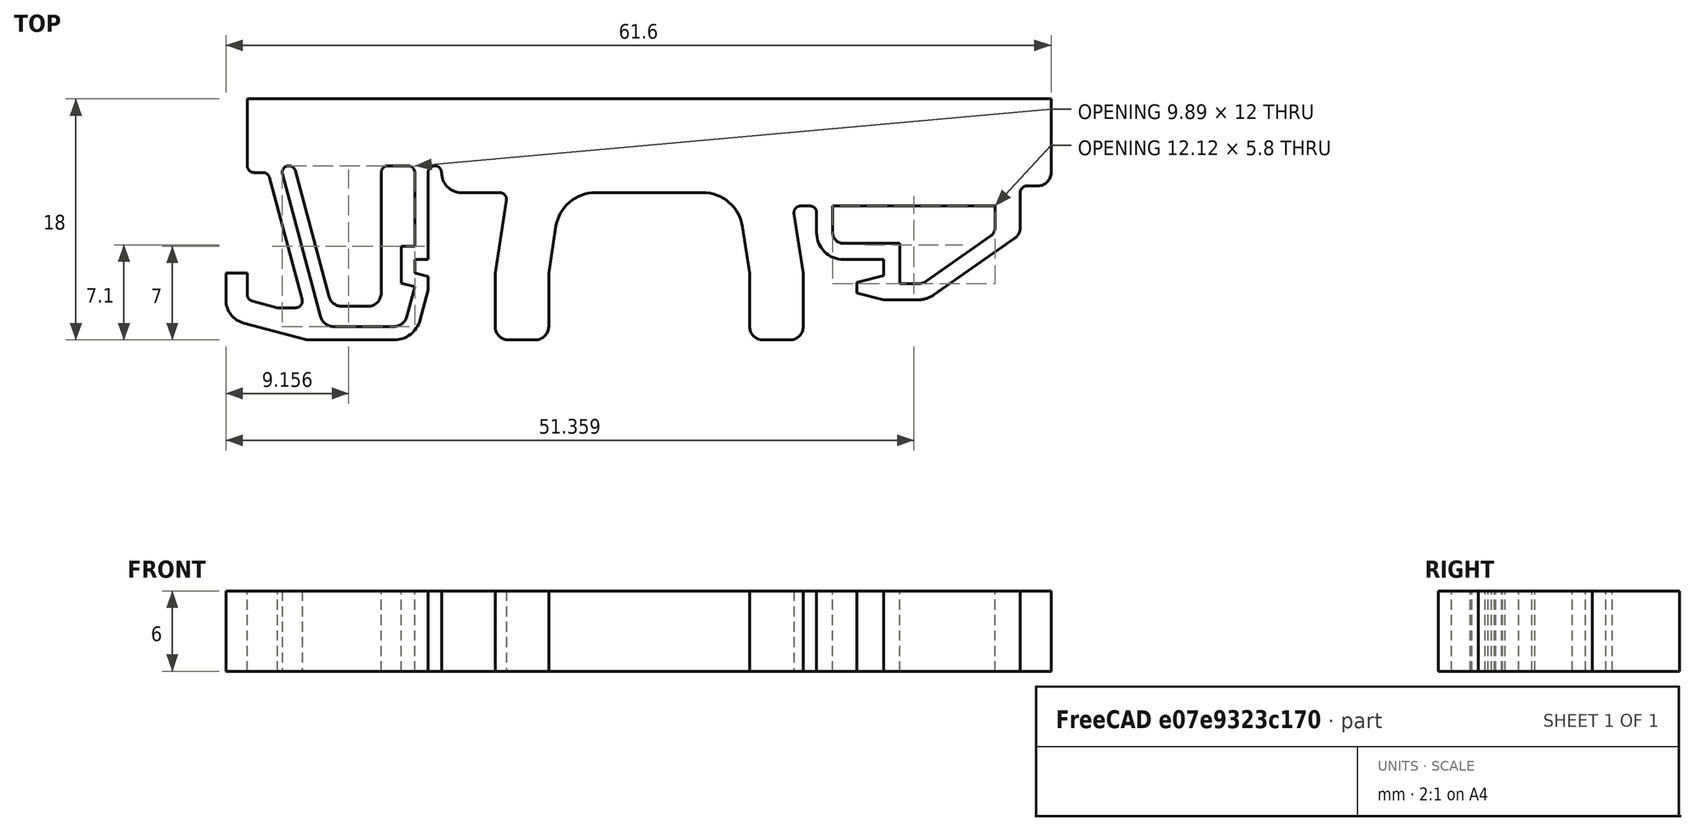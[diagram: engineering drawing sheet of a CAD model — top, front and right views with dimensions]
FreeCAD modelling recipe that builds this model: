
FCSTD DOCUMENT  (FreeCAD 0.21R33668 +26 (Git))
Label: din_rail_spacer_small_6
License: All rights reserved
LicenseURL: http://en.wikipedia.org/wiki/All_rights_reserved
objects: Sketcher::SketchObject×1, PartDesign::Pad×1, PartDesign::Body×1
note: 4 computed .brp shape members not serialized (recipe doc carries the construction recipe); baked Part::Feature solids carry a one-line shape summary decoded from their .brp

FEATURE [Sketcher::SketchObject] Sketch
  FullyConstrained = true
  MapMode = 5
  Support = -> [XY_Plane]
  sketch-geometry (97):
    g0: LineSegment StartX=30 StartY=12 StartZ=0 EndX=-30 EndY=12 EndZ=0
    g1: LineSegment StartX=-30 StartY=12 StartZ=0 EndX=-30 EndY=7 EndZ=0
    g2: ArcOfCircle CenterX=-29.5 CenterY=7 CenterZ=0 NormalX=0 NormalY=0 NormalZ=1 AngleXU=0 Radius=0.5 StartAngle=3.14159 EndAngle=4.71239
    g3: ArcOfCircle CenterX=-28.8294 CenterY=6 CenterZ=0 NormalX=0 NormalY=0 NormalZ=1 AngleXU=0 Radius=0.5 StartAngle=0.261799 EndAngle=1.5708
    g4: LineSegment StartX=-28.3464 StartY=6.12941 StartZ=0 EndX=-25.9081 EndY=-2.97059 EndZ=0
    g5: ArcOfCircle CenterX=-26.3911 CenterY=-3.1 CenterZ=0 NormalX=0 NormalY=0 NormalZ=1 AngleXU=0 Radius=0.5 StartAngle=4.71239 EndAngle=6.54498
    g6: ArcOfCircle CenterX=-29.5 CenterY=-2.61451 CenterZ=0 NormalX=0 NormalY=0 NormalZ=1 AngleXU=0 Radius=0.5 StartAngle=3.14159 EndAngle=4.45059
    g7: LineSegment StartX=-30 StartY=-2.61451 StartZ=0 EndX=-30 EndY=-1 EndZ=0
    g8: LineSegment StartX=-30 StartY=-1 StartZ=0 EndX=-31.6 EndY=-1 EndZ=0
    g9: LineSegment StartX=-31.6 StartY=-1 StartZ=0 EndX=-31.6 EndY=-3 EndZ=0
    g10: ArcOfCircle CenterX=-29.8 CenterY=-3 CenterZ=0 NormalX=0 NormalY=0 NormalZ=1 AngleXU=0 Radius=1.8 StartAngle=3.14159 EndAngle=4.45059
    g11: LineSegment StartX=-30.2659 StartY=-4.73867 StartZ=0 EndX=-25.6857 EndY=-5.96593 EndZ=0
    g12: ArcOfCircle CenterX=-25.4269 CenterY=-5 CenterZ=0 NormalX=0 NormalY=0 NormalZ=1 AngleXU=0 Radius=1 StartAngle=4.45059 EndAngle=4.71239
    g13: LineSegment StartX=-25.4269 StartY=-6 StartZ=0 EndX=-19.0347 EndY=-6 EndZ=0
    g14: ArcOfCircle CenterX=-19.0347 CenterY=-4 CenterZ=0 NormalX=0 NormalY=0 NormalZ=1 AngleXU=0 Radius=2 StartAngle=4.71239 EndAngle=6.02139
    g15: LineSegment StartX=-17.1028 StartY=-4.51764 StartZ=0 EndX=-16.5 EndY=-2.26795 EndZ=0
    g16: LineSegment StartX=-16.5 StartY=-2.26795 StartZ=0 EndX=-16.5 EndY=-1.26795 EndZ=0
    g17: LineSegment StartX=-16.5 StartY=-1.26795 StartZ=0 EndX=-17.5 EndY=-1 EndZ=0
    g18: LineSegment StartX=-17.5 StartY=-1 StartZ=0 EndX=-17.5 EndY=0 EndZ=0
    g19: LineSegment StartX=-17.5 StartY=0 StartZ=0 EndX=-16.5 EndY=0 EndZ=0
    g20: LineSegment StartX=-16.5 StartY=0 StartZ=0 EndX=-16.5 EndY=6.5 EndZ=0
    g21: ArcOfCircle CenterX=-16 CenterY=6.5 CenterZ=0 NormalX=0 NormalY=0 NormalZ=1 AngleXU=0 Radius=0.5 StartAngle=0 EndAngle=3.14159
    g22: ArcOfCircle CenterX=-14 CenterY=6.5 CenterZ=0 NormalX=0 NormalY=0 NormalZ=1 AngleXU=0 Radius=1.5 StartAngle=3.14159 EndAngle=4.71239
    g23: LineSegment StartX=-14 StartY=5 StartZ=0 EndX=-11.1548 EndY=5 EndZ=0
    g24: ArcOfCircle CenterX=-11.1548 CenterY=4.5 CenterZ=0 NormalX=0 NormalY=0 NormalZ=1 AngleXU=0 Radius=0.5 StartAngle=6.12964 EndAngle=7.85398
    g25: LineSegment StartX=-10.6606 StartY=4.42353 StartZ=0 EndX=-11.5 EndY=-1 EndZ=0
    g26: LineSegment StartX=-11.5 StartY=-1 StartZ=0 EndX=-11.5 EndY=-5 EndZ=0
    g27: ArcOfCircle CenterX=-10.5 CenterY=-5 CenterZ=0 NormalX=0 NormalY=0 NormalZ=1 AngleXU=0 Radius=1 StartAngle=3.14159 EndAngle=4.71239
    g28: LineSegment StartX=-10.5 StartY=-6 StartZ=0 EndX=-8.5 EndY=-6 EndZ=0
    g29: ArcOfCircle CenterX=-8.5 CenterY=-5 CenterZ=0 NormalX=0 NormalY=0 NormalZ=1 AngleXU=0 Radius=1 StartAngle=4.71239 EndAngle=6.28319
    g30: LineSegment StartX=-7.5 StartY=-5 StartZ=0 EndX=-7.5 EndY=-1 EndZ=0
    g31: LineSegment StartX=-7.5 StartY=-1 StartZ=0 EndX=-6.96471 EndY=2.45882 EndZ=0
    g32: ArcOfCircle CenterX=-4 CenterY=2 CenterZ=0 NormalX=0 NormalY=0 NormalZ=1 AngleXU=0 Radius=3 StartAngle=1.5708 EndAngle=2.98805
    g33: LineSegment StartX=-4 StartY=5 StartZ=0 EndX=4 EndY=5 EndZ=0
    g34: ArcOfCircle CenterX=4 CenterY=2 CenterZ=0 NormalX=0 NormalY=0 NormalZ=1 AngleXU=0 Radius=3 StartAngle=0.153544 EndAngle=1.5708
    g35: LineSegment StartX=6.96471 StartY=2.45882 StartZ=0 EndX=7.5 EndY=-1 EndZ=0
    g36: LineSegment StartX=7.5 StartY=-1 StartZ=0 EndX=7.5 EndY=-5 EndZ=0
    g37: ArcOfCircle CenterX=8.5 CenterY=-5 CenterZ=0 NormalX=0 NormalY=0 NormalZ=1 AngleXU=0 Radius=1 StartAngle=3.14159 EndAngle=4.71239
    g38: LineSegment StartX=8.5 StartY=-6 StartZ=0 EndX=10.5 EndY=-6 EndZ=0
    g39: ArcOfCircle CenterX=10.5 CenterY=-5 CenterZ=0 NormalX=0 NormalY=0 NormalZ=1 AngleXU=0 Radius=1 StartAngle=4.71239 EndAngle=6.28319
    g40: LineSegment StartX=11.5 StartY=-5 StartZ=0 EndX=11.5 EndY=-1 EndZ=0
    g41: LineSegment StartX=11.5 StartY=-1 StartZ=0 EndX=10.8154 EndY=3.42353 EndZ=0
    g42: LineSegment StartX=12.5 StartY=3.5 StartZ=0 EndX=12.5 EndY=2 EndZ=0
    g43: ArcOfCircle CenterX=14.5 CenterY=2 CenterZ=0 NormalX=0 NormalY=0 NormalZ=1 AngleXU=0 Radius=2 StartAngle=3.14159 EndAngle=4.71239
    g44: LineSegment StartX=14.5 StartY=0 StartZ=0 EndX=17.5 EndY=0 EndZ=0
    g45: LineSegment StartX=17.5 StartY=0 StartZ=0 EndX=17.5 EndY=-1.2 EndZ=0
    g46: LineSegment StartX=17.5 StartY=-1.2 StartZ=0 EndX=15.5 EndY=-1.7 EndZ=0
    g47: LineSegment StartX=15.5 StartY=-1.7 StartZ=0 EndX=15.5 EndY=-2.5 EndZ=0
    g48: LineSegment StartX=15.5 StartY=-2.5 StartZ=0 EndX=17.5 EndY=-3 EndZ=0
    g49: LineSegment StartX=17.5 StartY=-3 StartZ=0 EndX=20.1 EndY=-3 EndZ=0
    g50: ArcOfCircle CenterX=20.1 CenterY=-1 CenterZ=0 NormalX=0 NormalY=0 NormalZ=1 AngleXU=0 Radius=2 StartAngle=4.71239 EndAngle=5.32325
    g51: LineSegment StartX=21.2472 StartY=-2.6383 StartZ=0 EndX=27.2727 EndY=1.58085 EndZ=0
    g52: LineSegment StartX=30 StartY=6.5 StartZ=0 EndX=30 EndY=12 EndZ=0
    g53: LineSegment StartX=-23.8943 StartY=-2.75882 StartZ=0 EndX=-26.4099 EndY=6.62941 EndZ=0
    g54: ArcOfCircle CenterX=-26.8928 CenterY=6.5 CenterZ=0 NormalX=0 NormalY=0 NormalZ=1 AngleXU=0 Radius=0.5 StartAngle=0.261799 EndAngle=3.40339
    g55: LineSegment StartX=-27.3758 StartY=6.37059 StartZ=0 EndX=-24.5276 EndY=-4.25882 EndZ=0
    g56: ArcOfCircle CenterX=-23.5617 CenterY=-4 CenterZ=0 NormalX=0 NormalY=0 NormalZ=1 AngleXU=0 Radius=1 StartAngle=3.40339 EndAngle=4.71239
    g57: LineSegment StartX=-23.5617 StartY=-5 StartZ=0 EndX=-19.0617 EndY=-5 EndZ=0
    g58: ArcOfCircle CenterX=-19.0617 CenterY=-4 CenterZ=0 NormalX=0 NormalY=0 NormalZ=1 AngleXU=0 Radius=1 StartAngle=4.71239 EndAngle=6.02139
    g59: LineSegment StartX=-18.0958 StartY=-4.25882 StartZ=0 EndX=-17.5 EndY=-2.03528 EndZ=0
    g60: LineSegment StartX=-17.5 StartY=-2.03528 StartZ=0 EndX=-18.5 EndY=-1.76733 EndZ=0
    g61: LineSegment StartX=-18.5 StartY=-1.76733 StartZ=0 EndX=-18.5 EndY=1 EndZ=0
    g62: LineSegment StartX=-18.5 StartY=1 StartZ=0 EndX=-17.5 EndY=1 EndZ=0
    g63: LineSegment StartX=-17.5 StartY=1 StartZ=0 EndX=-17.5 EndY=6.5 EndZ=0
    g64: ArcOfCircle CenterX=-18 CenterY=6.5 CenterZ=0 NormalX=0 NormalY=0 NormalZ=1 AngleXU=0 Radius=0.5 StartAngle=0 EndAngle=1.5708
    g65: LineSegment StartX=-18 StartY=7 StartZ=0 EndX=-19.5 EndY=7 EndZ=0
    g66: ArcOfCircle CenterX=-19.5 CenterY=6.5 CenterZ=0 NormalX=0 NormalY=0 NormalZ=1 AngleXU=0 Radius=0.5 StartAngle=1.5708 EndAngle=3.14159
    g67: LineSegment StartX=-20 StartY=6.5 StartZ=0 EndX=-20 EndY=-2.5 EndZ=0
    g68: ArcOfCircle CenterX=-21 CenterY=-2.5 CenterZ=0 NormalX=0 NormalY=0 NormalZ=1 AngleXU=0 Radius=1 StartAngle=4.71239 EndAngle=6.28319
    g69: LineSegment StartX=-21 StartY=-3.5 StartZ=0 EndX=-22.9284 EndY=-3.5 EndZ=0
    g70: ArcOfCircle CenterX=-22.9284 CenterY=-2.5 CenterZ=0 NormalX=0 NormalY=0 NormalZ=1 AngleXU=0 Radius=1 StartAngle=3.40339 EndAngle=4.71239
    g71: LineSegment StartX=25.8188 StartY=4 StartZ=0 EndX=13.7 EndY=4 EndZ=0
    g72: LineSegment StartX=13.7 StartY=4 StartZ=0 EndX=13.7 EndY=2 EndZ=0
    g73: ArcOfCircle CenterX=14.5 CenterY=2 CenterZ=0 NormalX=0 NormalY=0 NormalZ=1 AngleXU=0 Radius=0.8 StartAngle=3.14159 EndAngle=4.71239
    g74: LineSegment StartX=14.5 StartY=1.2 StartZ=0 EndX=18.7 EndY=1.2 EndZ=0
    g75: LineSegment StartX=18.7 StartY=1.2 StartZ=0 EndX=18.7 EndY=-1.8 EndZ=0
    g76: LineSegment StartX=18.7 StartY=-1.8 StartZ=0 EndX=20.1 EndY=-1.8 EndZ=0
    g77: ArcOfCircle CenterX=20.1 CenterY=-0.8 CenterZ=0 NormalX=0 NormalY=0 NormalZ=1 AngleXU=0 Radius=1 StartAngle=4.71239 EndAngle=5.32325
    g78: LineSegment StartX=20.6736 StartY=-1.61915 StartZ=0 EndX=25.4776 EndY=1.74468 EndZ=0
    g79: ArcOfCircle CenterX=25.0188 CenterY=2.4 CenterZ=0 NormalX=0 NormalY=0 NormalZ=1 AngleXU=0 Radius=0.8 StartAngle=5.32325 EndAngle=6.28319
    g80: LineSegment StartX=25.8188 StartY=2.4 StartZ=0 EndX=25.8188 EndY=4 EndZ=0
    g81: LineSegment StartX=-30 StartY=7 StartZ=0 EndX=30 EndY=7 EndZ=0
    g82: LineSegment StartX=-29.6294 StartY=-3.09747 StartZ=0 EndX=-27.754 EndY=-3.6 EndZ=0
    g83: LineSegment StartX=-27.754 StartY=-3.6 StartZ=0 EndX=-26.3911 EndY=-3.6 EndZ=0
    g84: LineSegment StartX=-29.5 StartY=6.5 StartZ=0 EndX=-28.8294 EndY=6.5 EndZ=0
    g85: LineSegment StartX=11.3095 StartY=4 StartZ=0 EndX=12 EndY=4 EndZ=0
    g86: ArcOfCircle CenterX=11.3095 CenterY=3.5 CenterZ=0 NormalX=0 NormalY=0 NormalZ=1 AngleXU=0 Radius=0.5 StartAngle=1.5708 EndAngle=3.29514
    g87: GeomPoint X=10.7262 Y=4 Z=0
    g88: ArcOfCircle CenterX=12 CenterY=3.5 CenterZ=0 NormalX=0 NormalY=0 NormalZ=1 AngleXU=0 Radius=0.5 StartAngle=0 EndAngle=1.5708
    g89: GeomPoint X=12.5 Y=4 Z=0
    g90: LineSegment StartX=29 StartY=5.5 StartZ=0 EndX=28.1992 EndY=5.5 EndZ=0
    g91: ArcOfCircle CenterX=26.6992 CenterY=2.4 CenterZ=0 NormalX=0 NormalY=0 NormalZ=1 AngleXU=0 Radius=1 StartAngle=5.32325 EndAngle=6.28319
    g92: ArcOfCircle CenterX=29 CenterY=6.5 CenterZ=0 NormalX=0 NormalY=0 NormalZ=1 AngleXU=0 Radius=1 StartAngle=4.71239 EndAngle=6.28319
    g93: GeomPoint X=30 Y=5.5 Z=0
    g94: LineSegment StartX=27.6992 StartY=2.4 StartZ=0 EndX=27.6992 EndY=5 EndZ=0
    g95: ArcOfCircle CenterX=28.1992 CenterY=5 CenterZ=0 NormalX=0 NormalY=0 NormalZ=1 AngleXU=0 Radius=0.5 StartAngle=1.5708 EndAngle=3.14159
    g96: GeomPoint X=0 Y=12 Z=0
  constraints (251):
    c: Coincident(g0,g1)
    c: Vertical(g1)
    c: Tangent(g1,g2) = -1.5708
    c: Tangent(g4,g5) = 1.5708
    c: Vertical(g7)
    c: Coincident(g7,g8)
    c: Horizontal(g8)
    c: Coincident(g8,g9)
    c: Vertical(g9)
    c: Tangent(g9,g10) = -1.5708
    c: Tangent(g11,g12) = -1.5708
    c: Horizontal(g13)
    c: Tangent(g13,g14) = -1.5708
    c: Coincident(g15,g16)
    c: Vertical(g16)
    c: Coincident(g16,g17)
    c: Coincident(g17,g18)
    c: PointOnObject(g18,g-1)
    c: Vertical(g18)
    c: Coincident(g18,g19)
    c: PointOnObject(g19,g-1)
    c: Coincident(g19,g20)
    c: Vertical(g20)
    c: Tangent(g20,g21) = 1.5708
    c: Tangent(g21,g22) = 1.5708
    c: Horizontal(g23)
    c: Tangent(g23,g24) = 1.5708
    c: Coincident(g25,g26)
    c: Vertical(g26)
    c: Tangent(g26,g27) = -1.5708
    c: Horizontal(g28)
    c: Tangent(g28,g29) = -1.5708
    c: Vertical(g30)
    c: Coincident(g30,g31)
    c: Tangent(g31,g32) = 1.5708
    c: Tangent(g33,g34) = 1.5708
    c: Coincident(g35,g36)
    c: Vertical(g36)
    c: Tangent(g36,g37) = -1.5708
    c: Horizontal(g38)
    c: Tangent(g38,g39) = -1.5708
    c: Vertical(g40)
    c: Coincident(g40,g41)
    c: Vertical(g42)
    c: Tangent(g42,g43) = -1.5708
    c: Tangent(g43,g44) = -1.5708
    c: Coincident(g44,g45)
    c: Vertical(g45)
    c: Coincident(g45,g46)
    c: Coincident(g46,g47)
    c: Vertical(g47)
    c: Coincident(g47,g48)
    c: Coincident(g48,g49)
    c: Horizontal(g49)
    c: Tangent(g49,g50) = -1.5708
    c: Coincident(g52,g0)
    c: Vertical(g52)
    c: Tangent(g53,g54) = -1.5708
    c: Tangent(g55,g56) = -1.5708
    c: Horizontal(g57)
    c: Tangent(g57,g58) = -1.5708
    c: Coincident(g59,g60)
    c: Coincident(g60,g61)
    c: Vertical(g61)
    c: Coincident(g61,g62)
    c: Horizontal(g62)
    c: Coincident(g62,g63)
    c: Vertical(g63)
    c: Tangent(g63,g64) = -1.5708
    c: Tangent(g65,g66) = -1.5708
    c: Vertical(g67)
    c: Tangent(g67,g68) = 1.5708
    c: Horizontal(g69)
    c: Tangent(g69,g70) = 1.5708
    c: Horizontal(g71)
    c: Coincident(g71,g72)
    c: Vertical(g72)
    c: Tangent(g72,g73) = -1.5708
    c: Horizontal(g74)
    c: Coincident(g74,g75)
    c: Vertical(g75)
    c: Coincident(g75,g76)
    c: Horizontal(g76)
    c: Tangent(g76,g77) = -1.5708
    c: Tangent(g78,g79) = -1.5708
    c: Coincident(g80,g71)
    c: Vertical(g80)
    c: DistanceY(g1,g1) = 5  'Base_Width'
    c: Radius(g5) = 0.5
    c: Radius(g6) = 0.5
    c: DistanceY(g7,g-1) = 1
    c: DistanceX(g8,g8) = 1.6
    c: DistanceY(g9,g9) = 2
    c: Radius(g10) = 1.8
    c: Radius(g12) = 1
    c: Radius(g14) = 2
    c: Radius(g2) = 0.5
    c: Tangent(g3,g4) = 1.5708
    c: Tangent(g12,g13) = -1.5708
    c: Radius(g68) = 1
    c: Radius(g27) = 1
    c: Radius(g32) = 3
    c: Radius(g43) = 2
    c: Radius(g73) = 0.8
    c: Radius(g79) = 0.8
    c: Radius(g77) = 1
    c: Radius(g50) = 2
    c: Vertical(g62,g59)
    c: Vertical(g19,g16)
    c: Vertical(g62,g18)
    c: DistanceY(g57,g68) = 1.5
    c: DistanceY(g13,g57) = 1
    c: DistanceX(g66,g63) = 2.5
    c: DistanceX(g44,g74) = 1.2
    c: DistanceY(g44,g74) = 1.2
    c: Vertical(g45,g48)
    c: DistanceY(g48,g45) = 1.8
    c: Tangent(g27,g28) = -1.5708
    c: Tangent(g29,g30) = -1.5708
    c: DistanceX(g18,g44) = 35
    c: Symmetric(g18,g44,g-2)
    c: Tangent(g37,g38) = -1.5708
    c: Tangent(g39,g40) = -1.5708
    c: Equal(g39,g37)
    c: Equal(g37,g29)
    c: Equal(g29,g27)
    c: Equal(g32,g34)
    c: Equal(g40,g36)
    c: Equal(g36,g30)
    c: Equal(g30,g26)
    c: DistanceY(g-1,g28) = -6
    c: Symmetric(g29,g36,g-2)
    c: DistanceX(g29,g36) = 15
    c: DistanceX(g26,g29) = 4
    c: Equal(g28,g38)
    c: DistanceY(g26,g26) = 4
    c: DistanceY(g-1,g32) = 5
    c: Equal(g58,g68)
    c: Equal(g68,g70)
    c: Equal(g70,g56)
    c: DistanceY(g18,g18) = 1
    c: DistanceY(g45,g45) = 1.2
    c: Equal(g48,g46)
    c: DistanceY(g47,g47) = 0.8
    c: DistanceX(g46,g45) = 2
    c: DistanceX(g44,g44) = 3
    c: Tangent(g32,g33) = 1.5708
    c: Symmetric(g32,g33,g-2)
    c: DistanceX(g33,g33) = 8
    c: Parallel(g25,g31)
    c: Horizontal(g23,g32)
    c: Tangent(g66,g67) = -1.5708
    c: Tangent(g64,g65) = -1.5708
    c: Equal(g54,g66)
    c: Equal(g66,g64)
    c: Equal(g64,g21)
    c: Equal(g21,g24)
    c: Equal(g18,g19)
    c: Equal(g19,g62)
    c: Parallel(g15,g59)
    c: Angle(g17,g19) = 0.261799
    c: DistanceY(g-1,g13) = -6
    c: Distance(g75,g49) = 1.2
    c: Tangent(g79,g80) = -1.5708
    c: Tangent(g50,g51) = -1.5708
    c: Tangent(g77,g78) = -1.5708
    c: DistanceY(g80,g80) = 1.6
    c: Parallel(g78,g51)
    c: Vertical(g49,g76)
    c: Angle(g71,g78) = 0.610865
    c: Perpendicular(g17,g59)
    c: Equal(g16,g18)
    c: Tangent(g14,g15) = -1.5708
    c: Tangent(g58,g59) = -1.5708
    c: Parallel(g4,g55)
    c: Parallel(g55,g53)
    c: Angle(g67,g53) = 0.261799
    c: Tangent(g73,g74) = -1.5708
    c: Tangent(g10,g11) = -1.5708
    c: Tangent(g6,g7) = 1.5708
    c: Distance(g54,g4) = 1
    c: DistanceX(g57,g57) = 4.5
    c: Tangent(g56,g57) = -1.5708
    c: Parallel(g60,g17)
    c: Distance(g59,g17) = 1
    c: Tangent(g70,g53) = 1.5708
    c: Coincident(g81,g1)
    c: PointOnObject(g81,g52)
    c: Horizontal(g81)
    c: Tangent(g21,g81)
    c: Horizontal(g65)
    c: PointOnObject(g65,g81)
    c: Tangent(g54,g81)
    c: DistanceY(g-1,g1) = 7
    c: Parallel(g11,g17)
    c: Parallel(g82,g11)
    c: Distance(g6,g11) = 1.75
    c: Coincident(g83,g82)
    c: Horizontal(g83)
    c: Tangent(g82,g6) = -1.5708
    c: Tangent(g83,g5) = -1.5708
    c: DistanceY(g12,g5) = 2.4
    c: Vertical(g7,g1)
    c: DistanceX(g81,g81) = 60  'Total_Height'
    c: Tangent(g54,g55) = -1.5708
    c: DistanceY(g18,g62) = 1
    c: Tangent(g24,g25) = 1.5708
    c: Tangent(g34,g35) = 1.5708
    c: Tangent(g22,g23) = -1.5708
    c: Tangent(g68,g69) = 1.5708
    c: Equal(g2,g3)
    c: Horizontal(g22,g20)
    c: Tangent(g84,g2) = -1.5708
    c: Horizontal(g84)
    c: Tangent(g3,g84) = 1.5708
    c: Parallel(g35,g41)
    c: DistanceX(g42,g72) = 1.2
    c: Horizontal(g85)
    c: Horizontal(g89,g71)
    c: PointOnObject(g87,g41)
    c: PointOnObject(g87,g85)
    c: Tangent(g41,g86) = 1.5708
    c: Tangent(g85,g86) = 1.5708
    c: PointOnObject(g89,g42)
    c: PointOnObject(g89,g85)
    c: Tangent(g42,g88) = 1.5708
    c: Tangent(g85,g88) = 1.5708
    c: Equal(g86,g88)
    c: Equal(g86,g24)
    c: DistanceX(g76,g76) = 1.4
    c: DistanceY(g72,g72) = 2
    c: Radius(g86) = 0.5
    c: Horizontal(g90)
    c: PointOnObject(g93,g52)
    c: PointOnObject(g93,g90)
    c: Tangent(g52,g92) = -1.5708
    c: Tangent(g90,g92) = 1.5708
    c: Radius(g92) = 1
    c: Tangent(g91,g51) = -1.5708
    c: Radius(g91) = 1
    c: Horizontal(g0)
    c: Horizontal(g79,g91)
    c: DistanceY(g52,g81) = 0.5
    c: Vertical(g94)
    c: Tangent(g94,g91) = -1.5708
    c: Tangent(g90,g95) = -1.5708
    c: Tangent(g94,g95) = 1.5708
    c: Radius(g95) = 0.5
    c: Symmetric(g0,g0,g96)
    c: DistanceX(g-2,g96) = 0  'Center_Offset'
    c: Horizontal(g44)
FEATURE [PartDesign::Pad] Pad  label="spacer"
  AllowMultiFace = false
  Direction = (0,0,1)
  Length = 6
  Length2 = 100
  Midplane = true
  Profile = -> Sketch
  ReferenceAxis = -> Sketch [N_Axis]
  Refine = true
  Type = 0
FEATURE [PartDesign::Body] Body  label="DIN-rail-clip-adjustable"
  Group = -> [Sketch,Pad]
  Origin = -> Origin
  Tip = -> Pad
